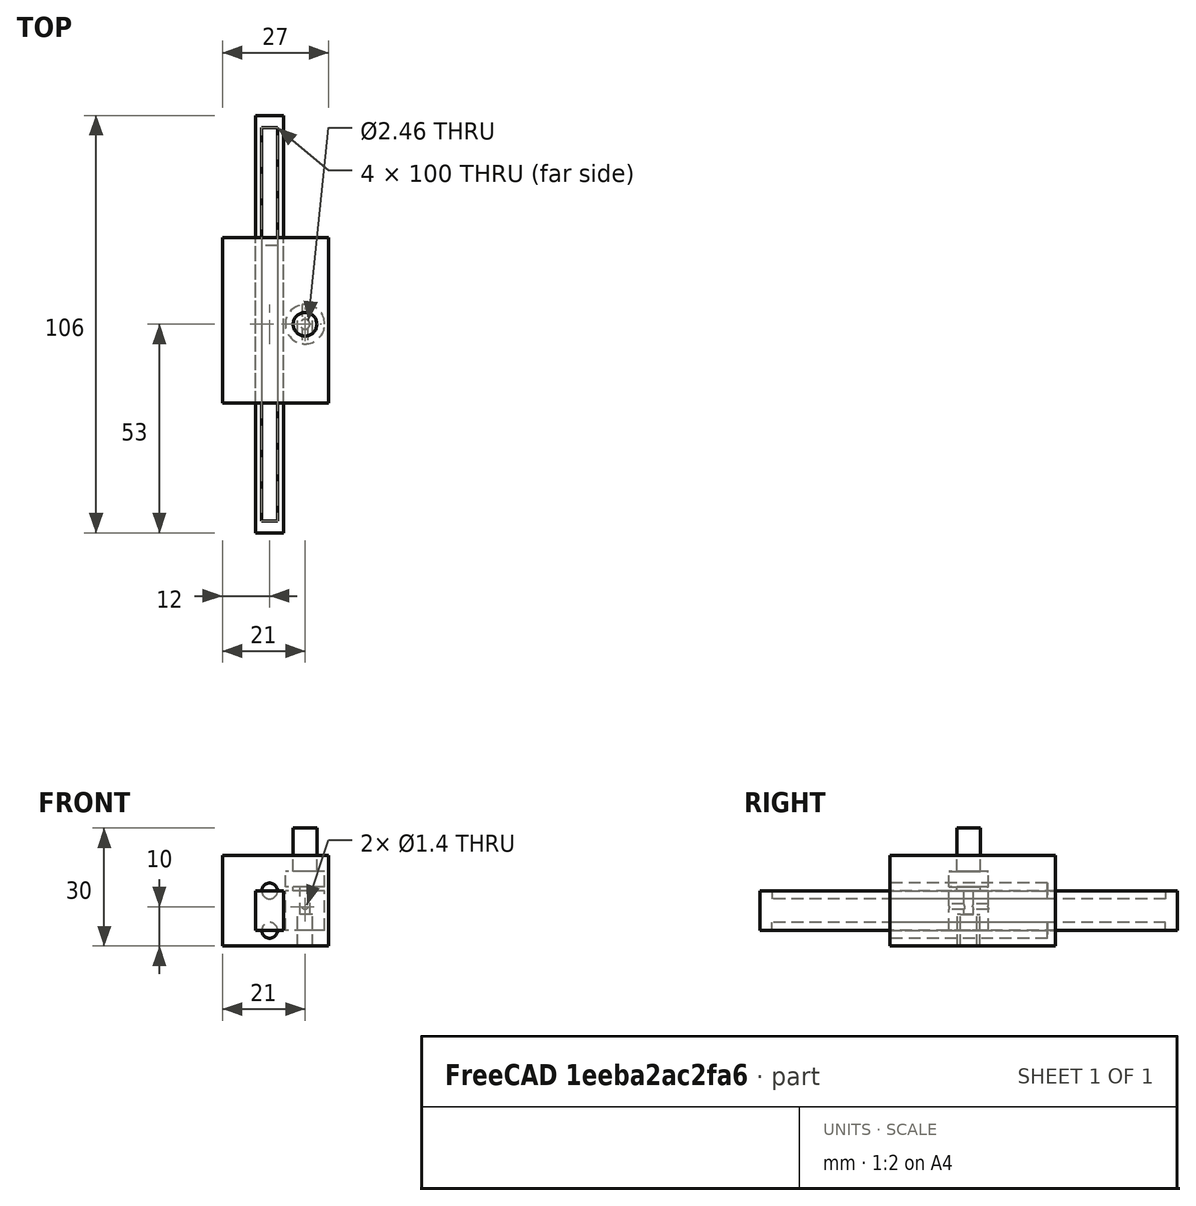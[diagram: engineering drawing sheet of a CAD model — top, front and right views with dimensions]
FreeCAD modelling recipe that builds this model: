
FCSTD DOCUMENT  (FreeCAD 0.15R4671 (Git))
Label: linear
License: All rights reserved
LicenseURL: http://en.wikipedia.org/wiki/All_rights_reserved
objects: Part::Cylinder×12, Part::Cut×5, Part::Box×4, Part::MultiCommon×2, Part::Fuse×1
note: 24 computed .brp shape members not serialized (recipe doc carries the construction recipe); baked Part::Feature solids carry a one-line shape summary decoded from their .brp

FEATURE [Part::Cylinder] Cylinder
  Angle = 360
  Height = 8
  Radius = 2.8
FEATURE [Part::Box] Box  label="Cube"
  Height = 10
  Length = 3.8
  Placement = pos=(-1.9,-5,-1) rot=(0,0,1;0rad)
  Width = 10
FEATURE [Part::MultiCommon] Common
  Placement = pos=(0,0,-4) rot=(0,0,1;0rad)
  Shapes = -> [Cylinder,Box]
FEATURE [Part::Cylinder] Cylinder001
  Angle = 360
  Height = 10
  Radius = 5
FEATURE [Part::Cylinder] Cylinder002
  Angle = 360
  Height = 14
  Placement = pos=(0,0,-2) rot=(0,0,1;0rad)
  Radius = 1.23
FEATURE [Part::Cylinder] Cylinder003
  Angle = 360
  Height = 10
  Placement = pos=(0,0,1) rot=(0,0,1;0rad)
  Radius = 3
FEATURE [Part::Fuse] Fusion
  Base = -> Cylinder001
  Tool = -> Cylinder003
FEATURE [Part::Cut] Cut
  Base = -> Fusion
  Tool = -> Cylinder002
FEATURE [Part::Cut] Cut001
  Base = -> Cut
  Tool = -> Common
FEATURE [Part::Cylinder] Cylinder004
  Angle = 360
  Height = 13
  Placement = pos=(0,7,6) rot=(1,0,0;1.5708rad)
  Radius = 0.7
FEATURE [Part::Cut] Cut002  label="drive-winder"
  Base = -> Cut001
  Tool = -> Cylinder004
FEATURE [Part::Cylinder] Cylinder005
  Angle = 360
  Height = 4
  Placement = pos=(0,0,11) rot=(0,0,1;0rad)
  Radius = 5
FEATURE [Part::Cylinder] Cylinder006
  Angle = 360
  Height = 8
  Radius = 2.8
FEATURE [Part::Box] Box001  label="Cube001"
  Height = 10
  Length = 3.8
  Placement = pos=(-1.9,-5,-1) rot=(0,0,1;0rad)
  Width = 10
FEATURE [Part::MultiCommon] Common001
  Placement = pos=(0,0,-4) rot=(0,0,1;0rad)
  Shapes = -> [Cylinder006,Box001]
FEATURE [Part::Cylinder] Cylinder007
  Angle = 360
  Height = 11
  Placement = pos=(0,0,15) rot=(0,0,1;0rad)
  Radius = 3
FEATURE [Part::Box] Box002  label="Cube002"
  Height = 23
  Length = 27
  Placement = pos=(-21,-20,-4) rot=(0,0,1;0rad)
  Width = 42
FEATURE [Part::Box] Box003  label="Cube003"
  Height = 10
  Length = 7
  Placement = pos=(-12.5,-53,0) rot=(0,0,1;0rad)
  Width = 106
FEATURE [Part::Cylinder] Cylinder008
  Angle = 360
  Height = 100
  Placement = pos=(-9,50,0) rot=(1,0,0;1.5708rad)
  Radius = 2
FEATURE [Part::Cylinder] Cylinder009
  Angle = 360
  Height = 100
  Placement = pos=(-9,50,10) rot=(1,0,0;1.5708rad)
  Radius = 2
FEATURE [Part::Cut] Cut003
  Base = -> Box003
  Tool = -> Cylinder008
FEATURE [Part::Cut] Cut004
  Base = -> Cut003
  Tool = -> Cylinder009
FEATURE [Part::Cylinder] Cylinder010
  Angle = 360
  Height = 40
  Placement = pos=(-9,20,0) rot=(1,0,0;1.5708rad)
  Radius = 2
FEATURE [Part::Cylinder] Cylinder011
  Angle = 360
  Height = 40
  Placement = pos=(-9,20,10) rot=(1,0,0;1.5708rad)
  Radius = 2
